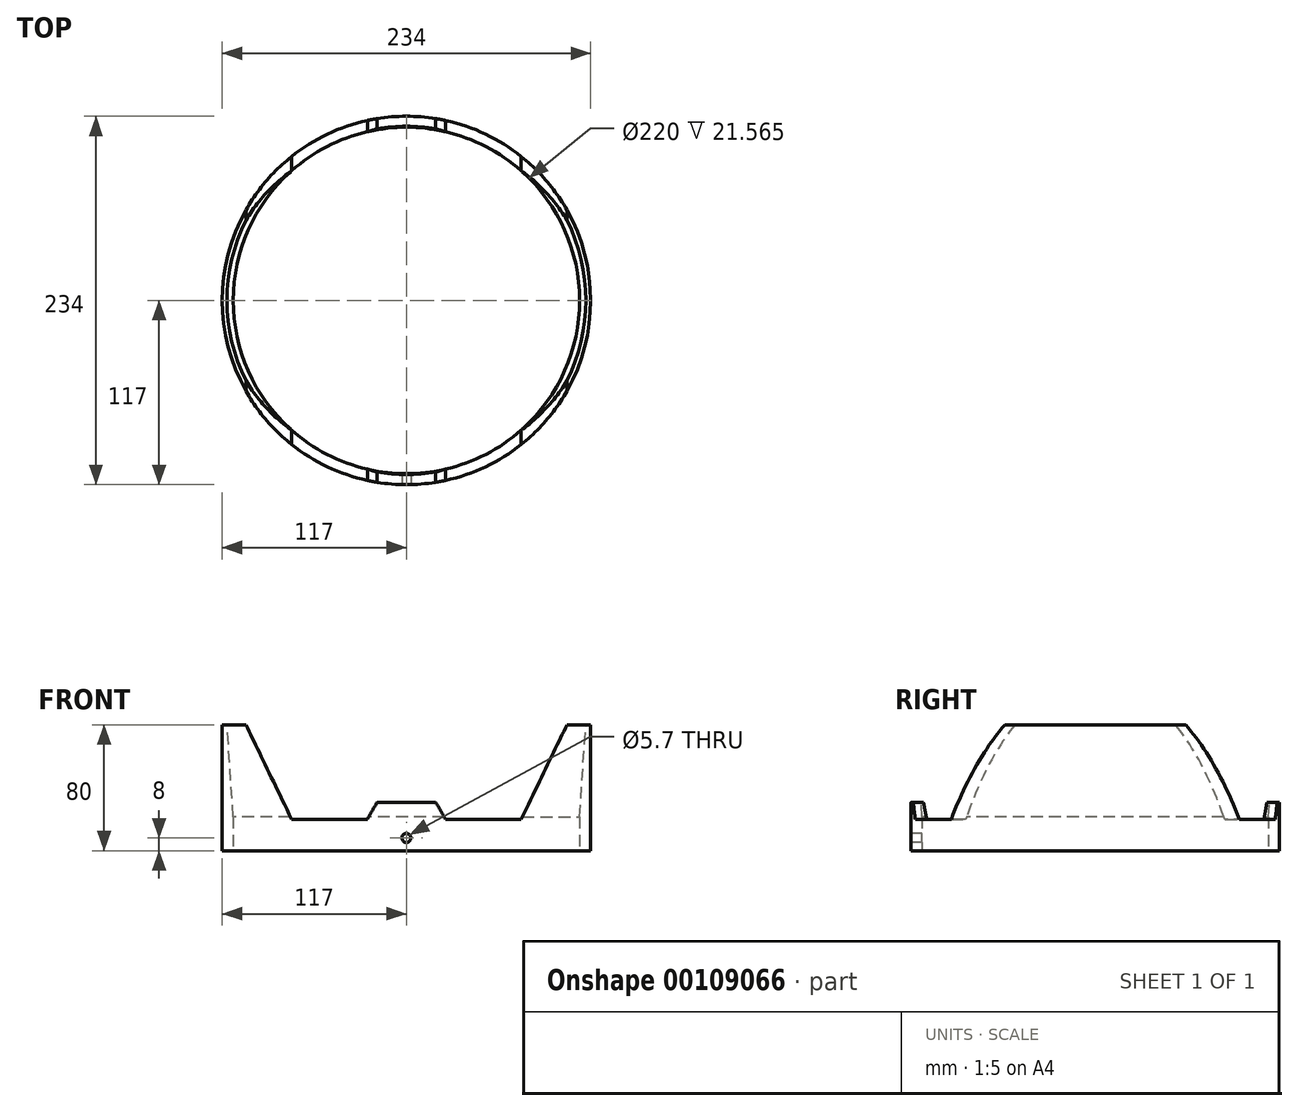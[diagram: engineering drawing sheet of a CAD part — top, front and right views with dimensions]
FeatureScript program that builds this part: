
annotation { "Feature Type Name" : "Feature", "Feature Type Description" : "" }
export const myFeature = defineFeature(function(context is Context, id is Id, definition is map)
    precondition{}
    {
        {
            var Q0;
            Q0=qCreatedBy(makeId("Top.planeOp"),FACE);
            var sketch = newSketch(context, id + "F0", { "sketchPlane" : qUnion([Q0])});
            skCircle(sketch, "E0", {"center": v(0, 0) * mm, "radius": 110 * mm});
            skCircle(sketch, "E1.0", {"center": v(0, 0) * mm, "radius": 117 * mm});
            skSolve(sketch);
        }
        {
            var Q0;
            Q0=makeQuery(id+"F0.imprint","IMPRINT",FACE,{"disambiguationData":[TD([[makeQuery(id+"F0.imprint","IMPRINT",EDGE,{"derivedFrom":sQuery(id+"F0.wireOp",EDGE,"E0")}),-1.0]])]});
            extrude(context, id + "F1", {"entities" : qUnion([Q0]), "flatOperationType" : FlatOperationType.REMOVE, "depth" : 80 * mm, "offsetDistance" : 25 * mm, "domain" : OperationDomain.MODEL});
        }
        {
            var Q0;
            Q0=qCreatedBy(makeId("Front.planeOp"),FACE);
            var sketch = newSketch(context, id + "F2", { "sketchPlane" : qUnion([Q0])});
            skLineSegment(sketch, "E2", {"start": v(-101.92, 80) * mm, "end": v(-72.95, 20) * mm});
            skLineSegment(sketch, "E3", {"start": v(-72.95, 20) * mm, "end": v(-24.84, 20) * mm});
            skLineSegment(sketch, "E4", {"start": v(-24.84, 20) * mm, "end": v(-18.62, 30.78) * mm});
            skLineSegment(sketch, "E5", {"start": v(-18.62, 30.78) * mm, "end": v(0, 30.78) * mm});
            skLineSegment(sketch, "E6", {"start": v(0, 30.78) * mm, "end": v(0, 80) * mm});
            skLineSegment(sketch, "E7", {"start": v(0, 80) * mm, "end": v(-101.92, 80) * mm});
            skLineSegment(sketch, "E8.MirrorCS", {"start": v(18.62, 30.78) * mm, "end": v(0, 30.78) * mm});
            skLineSegment(sketch, "E9.MirrorCS", {"start": v(24.84, 20) * mm, "end": v(18.62, 30.78) * mm});
            skLineSegment(sketch, "E10.MirrorCS", {"start": v(72.95, 20) * mm, "end": v(24.84, 20) * mm});
            skLineSegment(sketch, "E11.MirrorCS", {"start": v(101.92, 80) * mm, "end": v(72.95, 20) * mm});
            skLineSegment(sketch, "E12.MirrorCS", {"start": v(0, 80) * mm, "end": v(101.92, 80) * mm});
            skSolve(sketch);
        }
        {
            var Q0;
            Q0=makeQuery(id+"F2.imprint","IMPRINT",FACE,{"disambiguationData":[TD([[makeQuery(id+"F2.imprint","IMPRINT",EDGE,{"derivedFrom":sQuery(id+"F2.wireOp",EDGE,"E2")}),1.0]])]});
            var Q1;
            Q1=makeQuery(id+"F2.imprint","IMPRINT",FACE,{"disambiguationData":[TD([[makeQuery(id+"F2.imprint","IMPRINT",EDGE,{"derivedFrom":sQuery(id+"F2.wireOp",EDGE,"E6")}),-1.0]])]});
            extrude(context, id + "F3", {"entities" : qUnion([Q0, Q1]), "operationType" : NewBodyOperationType.REMOVE, "flatOperationType" : FlatOperationType.REMOVE, "depth" : 240 * mm, "offsetDistance" : 25 * mm, "domain" : OperationDomain.MODEL, "symmetric" : true});
        }
        {
            var Q0;
            Q0=qCreatedBy(makeId("Front.planeOp"),FACE);
            var sketch = newSketch(context, id + "F4", { "sketchPlane" : qUnion([Q0])});
            skPoint(sketch, "E13", {"position": v(0, 8) * mm});
            skSolve(sketch);
        }
        {
            var Q0;
            Q0=sQuery(id+"F4.wireOp",VERTEX,"E13");
            var Q1;
            Q1=makeQuery(id+"F1.opExtrude","SWEPT_BODY",BODY,{"disambiguationData":[OSD([sQuery(id+"F0.wireOp",EDGE,"E0"),sQuery(id+"F0.wireOp",EDGE,"E1.0")])]});
            hole(context, id + "F5", {"style" : HoleStyle.SIMPLE, "endStyle" : HoleEndStyle.THROUGH, "oppositeDirection" : true, "holeDiameter" : 5.7 * mm, "majorDiameter" : 5 * mm, "isTappedThrough" : true, "tappedDepth" : 12 * mm, "tapClearance" : 3, "locations" : qUnion([Q0]), "scope" : qUnion([Q1]), "startStyle" : HoleStartStyle.PART});
        }
        {
            var Q0;
            Q0=qCreatedBy(makeId("Front.planeOp"),FACE);
            var sketch = newSketch(context, id + "F6", { "sketchPlane" : qUnion([Q0])});
            skLineSegment(sketch, "E14", {"start": v(0, 19.14) * mm, "end": v(-109.84, 19.14) * mm});
            skLineSegment(sketch, "E15", {"start": v(-109.84, 19.14) * mm, "end": v(-114, 80.7) * mm});
            skLineSegment(sketch, "E16", {"start": v(-114, 80.7) * mm, "end": v(0, 80.7) * mm});
            skLineSegment(sketch, "E17", {"start": v(0, 80.7) * mm, "end": v(0, 19.14) * mm});
            skSolve(sketch);
        }
        {
            var Q0;
            Q0=makeQuery(id+"F6.imprint","IMPRINT",FACE,{"disambiguationData":[TD([[makeQuery(id+"F6.imprint","IMPRINT",EDGE,{"derivedFrom":sQuery(id+"F6.wireOp",EDGE,"E14")}),-1.0]])]});
            var Q1;
            Q1=sQuery(id+"F6.wireOp",EDGE,"E17");
            revolve(context, id + "F7", {"operationType" : NewBodyOperationType.REMOVE, "surfaceOperationType" : NewSurfaceOperationType.NEW, "entities" : qUnion([Q0]), "axis" : qUnion([Q1]), "revolveType" : RevolveType.FULL, "oppositeDirection" : true});
        }
    });
